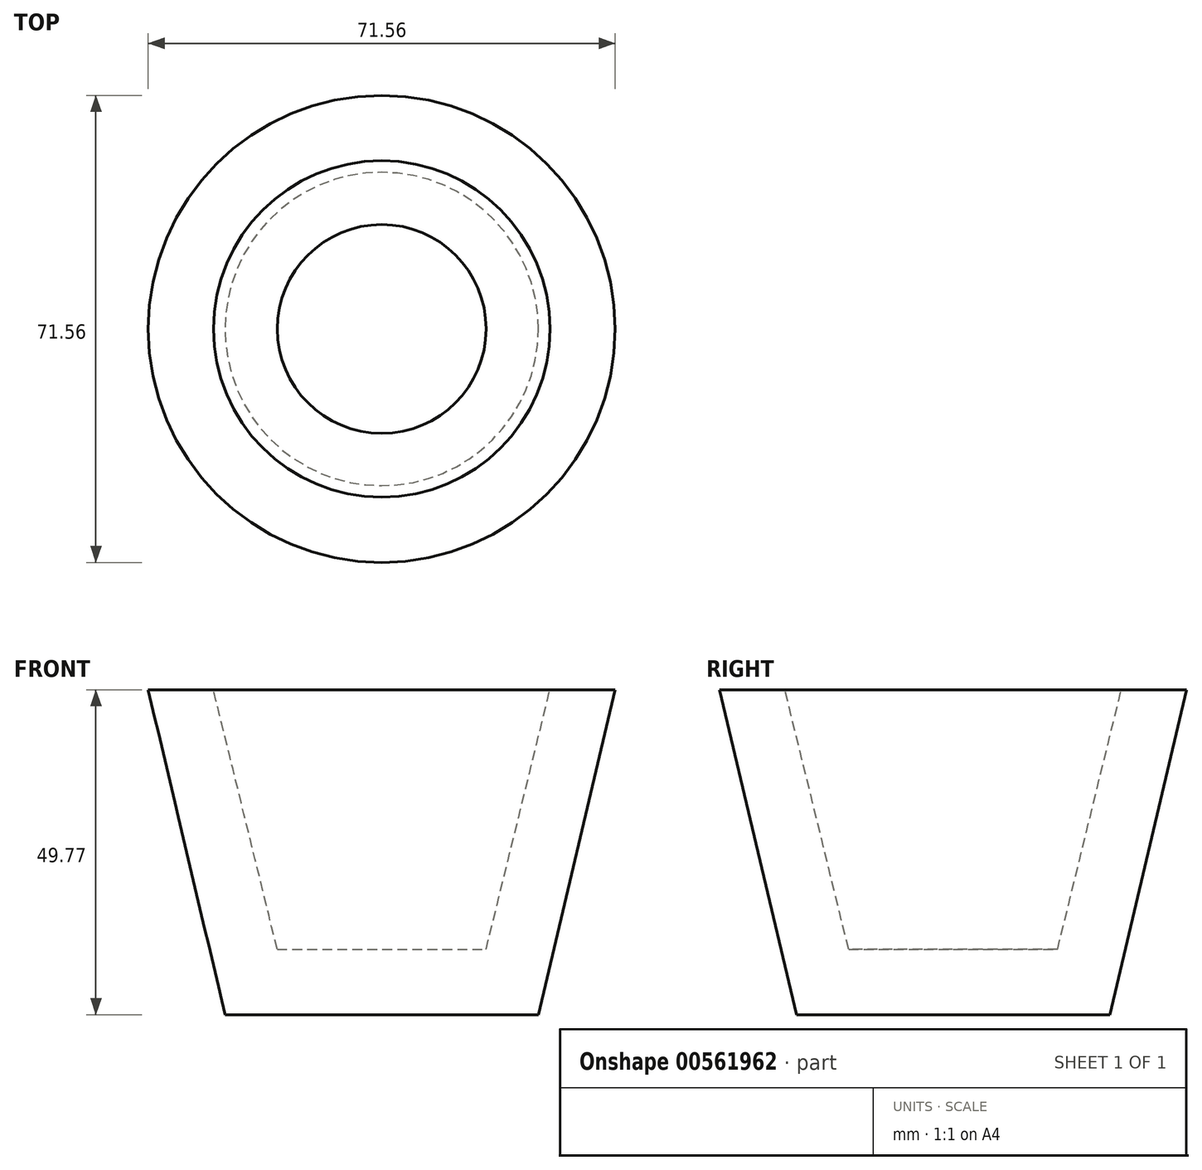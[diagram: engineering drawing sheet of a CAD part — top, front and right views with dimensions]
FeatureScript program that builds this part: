
annotation { "Feature Type Name" : "Feature", "Feature Type Description" : "" }
export const myFeature = defineFeature(function(context is Context, id is Id, definition is map)
    precondition{}
    {
        {
            var Q0;
            Q0=qCreatedBy(makeId("Front.planeOp"),FACE);
            var sketch = newSketch(context, id + "F0", { "sketchPlane" : qUnion([Q0])});
            skLineSegment(sketch, "E0", {"start": v(0, 0) * mm, "end": v(24, 0) * mm});
            skLineSegment(sketch, "E1", {"start": v(0, 0) * mm, "end": v(0, 49.77) * mm});
            skLineSegment(sketch, "E2", {"start": v(0, 49.77) * mm, "end": v(35.78, 49.77) * mm});
            skLineSegment(sketch, "E3", {"start": v(35.78, 49.77) * mm, "end": v(24, 0) * mm});
            skLineSegment(sketch, "E4", {"start": v(0, 10) * mm, "end": v(16, 10) * mm});
            skLineSegment(sketch, "E5", {"start": v(0, 10) * mm, "end": v(0, 49.77) * mm});
            skLineSegment(sketch, "E6", {"start": v(0, 49.77) * mm, "end": v(25.78, 49.77) * mm});
            skLineSegment(sketch, "E7", {"start": v(25.78, 49.77) * mm, "end": v(16, 10) * mm});
            skSolve(sketch);
        }
        {
            var Q0;
            Q0=makeQuery(id+"F0.imprint","IMPRINT",FACE,{"disambiguationData":[TD([[makeQuery(id+"F0.imprint","IMPRINT",EDGE,{"derivedFrom":sQuery(id+"F0.wireOp",EDGE,"E0")}),1.0]])]});
            var Q1;
            Q1=sQuery(id+"F0.wireOp",EDGE,"E5");
            revolve(context, id + "F1", {"entities" : qUnion([Q0]), "axis" : qUnion([Q1]), "revolveType" : RevolveType.FULL});
        }
    });
